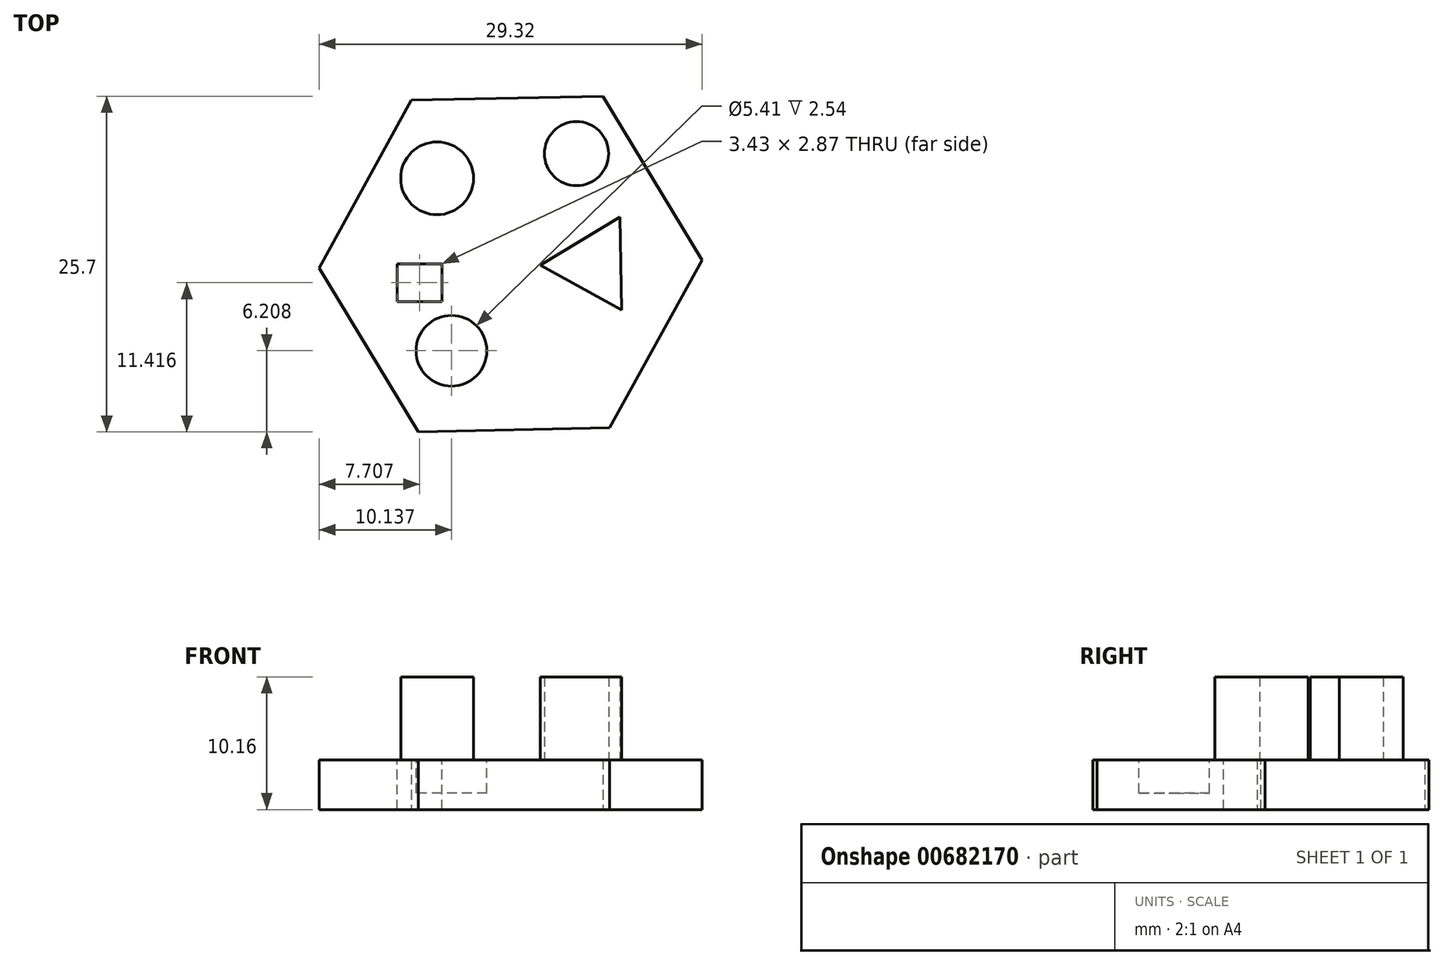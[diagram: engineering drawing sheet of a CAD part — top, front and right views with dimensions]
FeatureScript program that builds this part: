
annotation { "Feature Type Name" : "Feature", "Feature Type Description" : "" }
export const myFeature = defineFeature(function(context is Context, id is Id, definition is map)
    precondition{}
    {
        {
            var Q0;
            Q0=qCreatedBy(makeId("Top.planeOp"),FACE);
            var sketch = newSketch(context, id + "F0", { "sketchPlane" : qUnion([Q0])});
            skCircle(sketch, "E0.cCircle", {"center": v(0, 0) * mm, "radius": 12.7 * mm, "construction": true});
            skLineSegment(sketch, "E0.0", {"start": v(7.07, 12.85) * mm, "end": v(14.66, 0.3) * mm});
            skLineSegment(sketch, "E0.1", {"start": v(14.66, 0.3) * mm, "end": v(7.6, -12.55) * mm});
            skLineSegment(sketch, "E0.2", {"start": v(7.6, -12.55) * mm, "end": v(-7.07, -12.85) * mm});
            skLineSegment(sketch, "E0.3", {"start": v(-7.07, -12.85) * mm, "end": v(-14.66, -0.3) * mm});
            skLineSegment(sketch, "E0.4", {"start": v(-14.66, -0.3) * mm, "end": v(-7.6, 12.55) * mm});
            skLineSegment(sketch, "E0.5", {"start": v(-7.6, 12.55) * mm, "end": v(7.07, 12.85) * mm});
            skPoint(sketch, "E0.0.midPoint", {"position": v(10.87, 6.57) * mm});
            skSolve(sketch);
        }
        {
            var Q0;
            Q0=makeQuery(id+"F0.imprint","IMPRINT",FACE,{"disambiguationData":[TD([[makeQuery(id+"F0.imprint","IMPRINT",EDGE,{"derivedFrom":sQuery(id+"F0.wireOp",EDGE,"E0.0")}),-1.0]])]});
            extrude(context, id + "F1", {"entities" : qUnion([Q0]), "depth" : 3.8 * mm, "offsetDistance" : 25.4 * mm});
        }
        {
            var Q0;
            Q0=makeQuery(id+"F1.opExtrude","CAP_FACE",FACE,{"disambiguationData":[OSD([sQuery(id+"F0.wireOp",EDGE,"E0.0"),sQuery(id+"F0.wireOp",EDGE,"E0.1"),sQuery(id+"F0.wireOp",EDGE,"E0.2"),sQuery(id+"F0.wireOp",EDGE,"E0.3"),sQuery(id+"F0.wireOp",EDGE,"E0.4"),sQuery(id+"F0.wireOp",EDGE,"E0.5")])],"isStart":false});
            var sketch = newSketch(context, id + "F2", { "sketchPlane" : qUnion([Q0])});
            skCircle(sketch, "E1", {"center": v(-5.62, 6.56) * mm, "radius": 2.79 * mm});
            skCircle(sketch, "E2", {"center": v(5.05, 8.45) * mm, "radius": 2.45 * mm});
            skCircle(sketch, "E3.cCircle", {"center": v(6.38, 0) * mm, "radius": 2.06 * mm, "construction": true});
            skLineSegment(sketch, "E3.0", {"start": v(8.37, 3.6) * mm, "end": v(8.51, -3.52) * mm});
            skLineSegment(sketch, "E3.1", {"start": v(8.51, -3.52) * mm, "end": v(2.27, -0.08) * mm});
            skLineSegment(sketch, "E3.2", {"start": v(2.27, -0.08) * mm, "end": v(8.37, 3.6) * mm});
            skPoint(sketch, "E3.0.midPoint", {"position": v(8.44, 0.04) * mm});
            skSolve(sketch);
        }
        {
            var Q0;
            Q0 = qSketchRegion(id + "F2", true);
            extrude(context, id + "F3", {"entities" : qUnion([Q0]), "operationType" : NewBodyOperationType.ADD, "depth" : 6.35 * mm, "offsetDistance" : 25.4 * mm});
        }
        {
            var Q0;
            Q0=makeQuery(id+"F1.opExtrude","CAP_FACE",FACE,{"disambiguationData":[OSD([sQuery(id+"F0.wireOp",EDGE,"E0.0"),sQuery(id+"F0.wireOp",EDGE,"E0.1"),sQuery(id+"F0.wireOp",EDGE,"E0.2"),sQuery(id+"F0.wireOp",EDGE,"E0.3"),sQuery(id+"F0.wireOp",EDGE,"E0.4"),sQuery(id+"F0.wireOp",EDGE,"E0.5")])],"isStart":false});
            var sketch = newSketch(context, id + "F4", { "sketchPlane" : qUnion([Q0])});
            skLineSegment(sketch, "E4.bottom", {"start": v(-8.67, 0) * mm, "end": v(-5.24, 0) * mm});
            skLineSegment(sketch, "E4.top", {"start": v(-8.67, -2.87) * mm, "end": v(-5.24, -2.87) * mm});
            skLineSegment(sketch, "E4.left", {"start": v(-8.67, 0) * mm, "end": v(-8.67, -2.87) * mm});
            skLineSegment(sketch, "E4.right", {"start": v(-5.24, 0) * mm, "end": v(-5.24, -2.87) * mm});
            skCircle(sketch, "E5", {"center": v(-2.95, -6.9) * mm, "radius": 1.97 * mm});
            skSolve(sketch);
        }
        {
            var Q0;
            Q0=makeQuery(id+"F4.imprint","IMPRINT",FACE,{"disambiguationData":[TD([[makeQuery(id+"F4.imprint","IMPRINT",EDGE,{"derivedFrom":sQuery(id+"F4.wireOp",EDGE,"E4.bottom")}),-1.0]])]});
            extrude(context, id + "F5", {"entities" : qUnion([Q0]), "operationType" : NewBodyOperationType.REMOVE, "oppositeDirection" : true, "depth" : 5.08 * mm, "offsetDistance" : 25.4 * mm});
        }
        {
            var Q0;
            Q0=makeQuery(id+"F1.opExtrude","CAP_FACE",FACE,{"disambiguationData":[OSD([sQuery(id+"F0.wireOp",EDGE,"E0.0"),sQuery(id+"F0.wireOp",EDGE,"E0.1"),sQuery(id+"F0.wireOp",EDGE,"E0.2"),sQuery(id+"F0.wireOp",EDGE,"E0.3"),sQuery(id+"F0.wireOp",EDGE,"E0.4"),sQuery(id+"F0.wireOp",EDGE,"E0.5")])],"isStart":false});
            var sketch = newSketch(context, id + "F6", { "sketchPlane" : qUnion([Q0])});
            skCircle(sketch, "E6", {"center": v(-4.52, -6.64) * mm, "radius": 2.7 * mm});
            skSolve(sketch);
        }
        {
            var Q0;
            Q0=makeQuery(id+"F6.imprint","IMPRINT",FACE,{"disambiguationData":[TD([[makeQuery(id+"F6.imprint","IMPRINT",EDGE,{"derivedFrom":sQuery(id+"F6.wireOp",EDGE,"E6")}),1.0]])]});
            extrude(context, id + "F7", {"entities" : qUnion([Q0]), "operationType" : NewBodyOperationType.REMOVE, "oppositeDirection" : true, "depth" : 2.54 * mm, "offsetDistance" : 25.4 * mm});
        }
    });
